# Revit family: Electronics_Amplifier_Biamp_Tesira_XEL_4-Channel-1200W__
name_source: partatom
category: Communication Devices
units: mm (PartAtom-declared; Revit-internal decimal feet)

## family parameters
Cut with Voids When Loaded = Yes
Host = Face
Maintain Annotation Orientation = No
OmniClass Number = 23.85.10.11.14.14.17
OmniClass Title = Sound Amplifiers
Part Type = Normal
Room Calculation Point = No
Round Connector Dimension = Use Diameter
Shared = No

## types (2) — shared parameters
Altitude = 0-10,000 ft (0-3000m) MSL
Amplifier Topology = Class D
Apparent Load = 660 VA
Balanced Input Impedance = 8 kohm
Bridged = 8 ohm: 350W
Compliance = FCC Part 15B (USA) CE Marked (Europe) UL and C-UL listed (USA and Canada) RoHS Directive (Europe)
Connector Description = 100-240VAC 50/60Hz
Connectors = 2-pin, 0.3-inch Euroblock [up to 10 AWG]
Cooling = Variable speed fan
Crosstalk = > 80dB
Current = 6 A
Current Draw = 5.5–2.3A
Damping Factor = > 600
Default Elevation = 48 "
Depth = 17.4 "
Dual AVB/TSN Input = RJ-45 (CAT-5 or higher) inputs; primary and secondary
Dynamic Range = > 108dB
Frequency Response = +0/-0.5dB
Height = 3.5 "
Housing Material = Biamp - Metal - Silver
Humidity = 0-95% relative humidity (non-condensing)
Manufacturer = Biamp
Minimum Operational Load = 2 ohm
Network Connection = (2) Gigabit Ethernet with RJ-45 (Cat 5e and above)
Number of Channels = 4
Number of Poles = 1
Optional Analog Cards = Tesira EX-MOD cards: EIC-4, EIOC-4, EOC-4
Power Factor = 1
Product Documentation Link = https://downloads.biamp.com
Product Page URL = https://www.biamp.com
Product data url = https://www.bimobject.com
Single Channel = 4 ohm, 8 ohm: 175W
Single Channel Driven = 1200W
THD+N = 20Hz-20kHz, at rated power: < 0.02%
Temperature Range = 32 - 95° F (0 - 35° C)
Tesira_XEL = Yes
URL = https://www.biamp.com
Voltage = 120 V
Weight = 18.00 lbf
Width = 19 "

## per-type parameters (varying)
| type | All Channels Driven | Description | Model | Number of Power Banks |
| XEL 1200.1 | 1200W | TesiraXEL™ 1200.1 4-Channel, 1200W Amplifier (Single Asymmetric Bank) | TesiraXEL 1200.1 | 1 |
| XEL 1200.2 | 2400W | TesiraXEL™ 1200.2 4-Channel, 2400W Amplifier (Dual Asymmetric Banks) | TesiraXEL 1200. 2 | 2 |

## geometry (parser evidence)
native form markers: Sweep x2
no freeform markers — native parametric forms only
